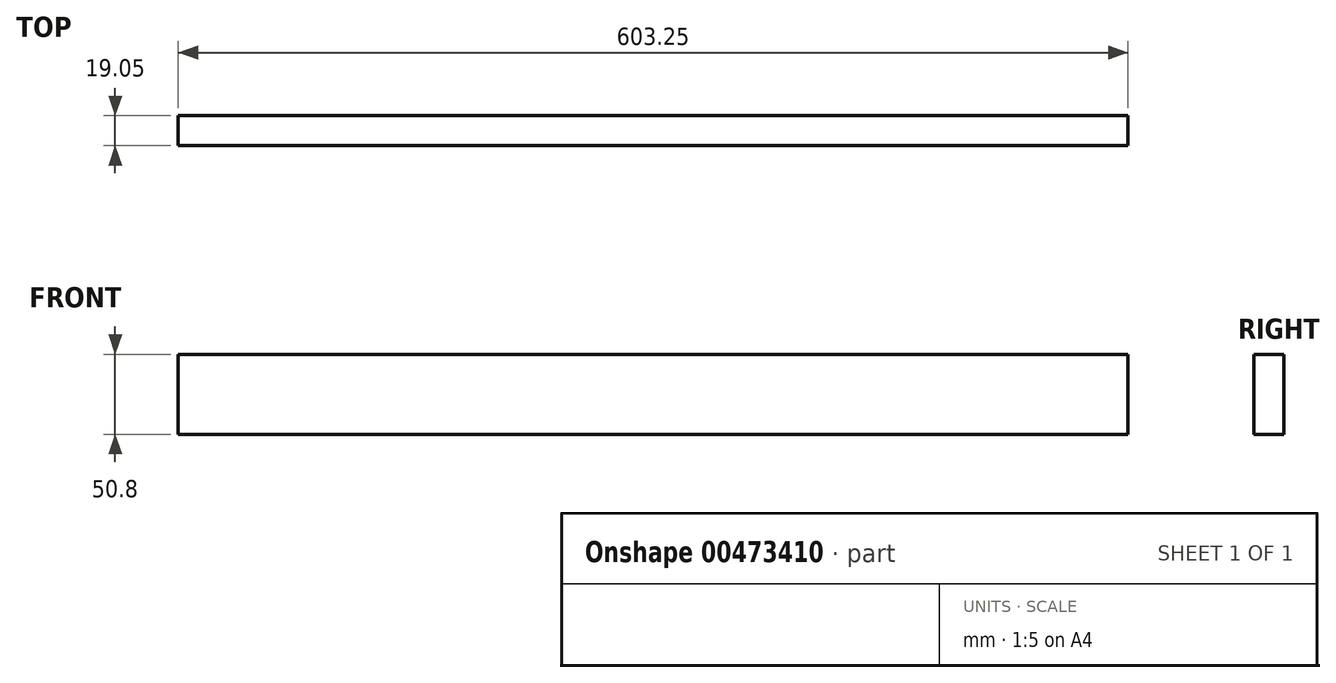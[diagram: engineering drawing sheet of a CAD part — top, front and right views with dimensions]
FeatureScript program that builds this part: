
annotation { "Feature Type Name" : "Feature", "Feature Type Description" : "" }
export const myFeature = defineFeature(function(context is Context, id is Id, definition is map)
    precondition{}
    {
        {
            var Q0;
            Q0=qCreatedBy(makeId("Front.planeOp"),FACE);
            var sketch = newSketch(context, id + "F0", { "sketchPlane" : qUnion([Q0])});
            skLineSegment(sketch, "E0.bottom", {"start": v(14.4, 54.83) * mm, "end": v(617.64, 54.83) * mm});
            skLineSegment(sketch, "E0.top", {"start": v(14.4, 4.03) * mm, "end": v(617.64, 4.03) * mm});
            skLineSegment(sketch, "E0.left", {"start": v(14.4, 54.83) * mm, "end": v(14.4, 4.03) * mm});
            skLineSegment(sketch, "E0.right", {"start": v(617.64, 54.83) * mm, "end": v(617.64, 4.03) * mm});
            skSolve(sketch);
        }
        {
            var Q0;
            Q0=makeQuery(id+"F0.imprint","IMPRINT",FACE,{"disambiguationData":[TD([[makeQuery(id+"F0.imprint","IMPRINT",EDGE,{"derivedFrom":sQuery(id+"F0.wireOp",EDGE,"E0.bottom")}),-1.0]])]});
            extrude(context, id + "F1", {"entities" : qUnion([Q0]), "depth" : 19.05 * mm});
        }
    });
